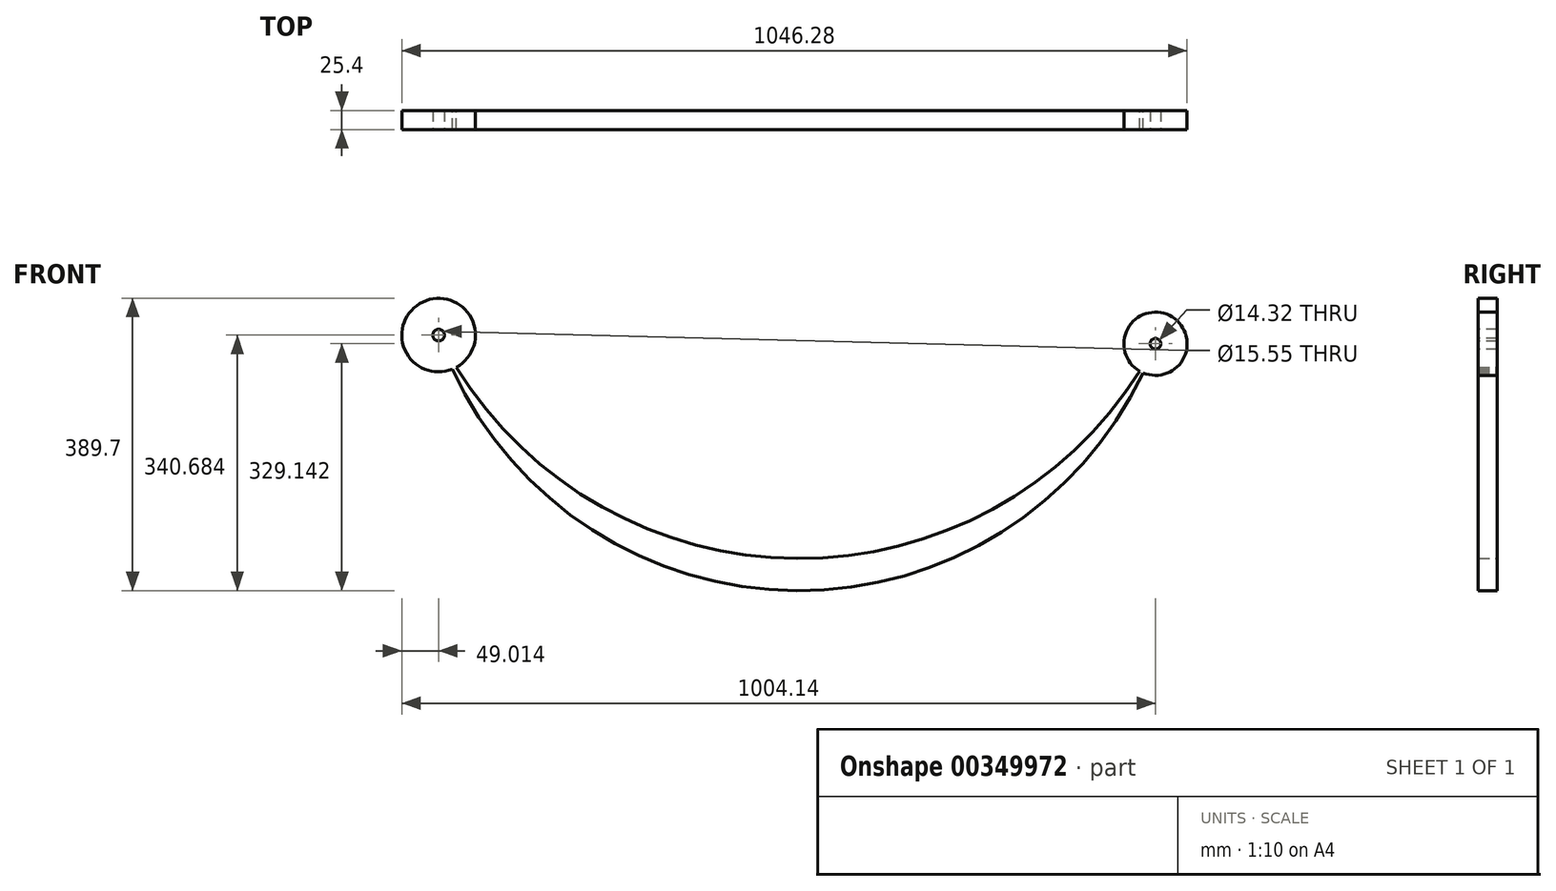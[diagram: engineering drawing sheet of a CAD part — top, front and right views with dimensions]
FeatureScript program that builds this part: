
annotation { "Feature Type Name" : "Feature", "Feature Type Description" : "" }
export const myFeature = defineFeature(function(context is Context, id is Id, definition is map)
    precondition{}
    {
        {
            var Q0;
            Q0=qCreatedBy(makeId("Front.planeOp"),FACE);
            var sketch = newSketch(context, id + "F0", { "sketchPlane" : qUnion([Q0])});
            skCircle(sketch, "E0", {"center": v(-444.92, 138.74) * mm, "radius": 49.01 * mm});
            skArc(sketch, "E1", {"start": v(-444.92, 138.74) * mm, "mid": v(29.12, -159.04) * mm, "end": v(510.21, 127.2) * mm});
            skCircle(sketch, "E2", {"center": v(510.21, 127.2) * mm, "radius": 42.14 * mm});
            skArc(sketch, "E3", {"start": v(-444.92, 138.74) * mm, "mid": v(28.6, -201.9) * mm, "end": v(510.21, 127.2) * mm});
            skSolve(sketch);
        }
        {
            var Q0;
            Q0 = qSketchRegion(id + "F0", true);
            extrude(context, id + "F1", {"entities" : qUnion([Q0]), "depth" : 25.4 * mm, "offsetDistance" : 25.4 * mm});
        }
        {
            var Q0;
            Q0=makeQuery(id+"F1.opExtrude","CAP_FACE",FACE,{"disambiguationData":[OSD([sQuery(id+"F0.wireOp",EDGE,"E0"),sQuery(id+"F0.wireOp",EDGE,"E1"),sQuery(id+"F0.wireOp",EDGE,"E2"),sQuery(id+"F0.wireOp",EDGE,"E3")])],"isStart":false});
            var sketch = newSketch(context, id + "F2", { "sketchPlane" : qUnion([Q0])});
            skCircle(sketch, "E4", {"center": v(-444.92, 138.74) * mm, "radius": 7.77 * mm});
            skCircle(sketch, "E5", {"center": v(510.21, 127.2) * mm, "radius": 7.16 * mm});
            skSolve(sketch);
        }
        {
            var Q0;
            Q0 = qSketchRegion(id + "F2", true);
            extrude(context, id + "F3", {"entities" : qUnion([Q0]), "operationType" : NewBodyOperationType.REMOVE, "oppositeDirection" : true, "depth" : 30.73 * mm, "offsetDistance" : 25.4 * mm});
        }
    });
